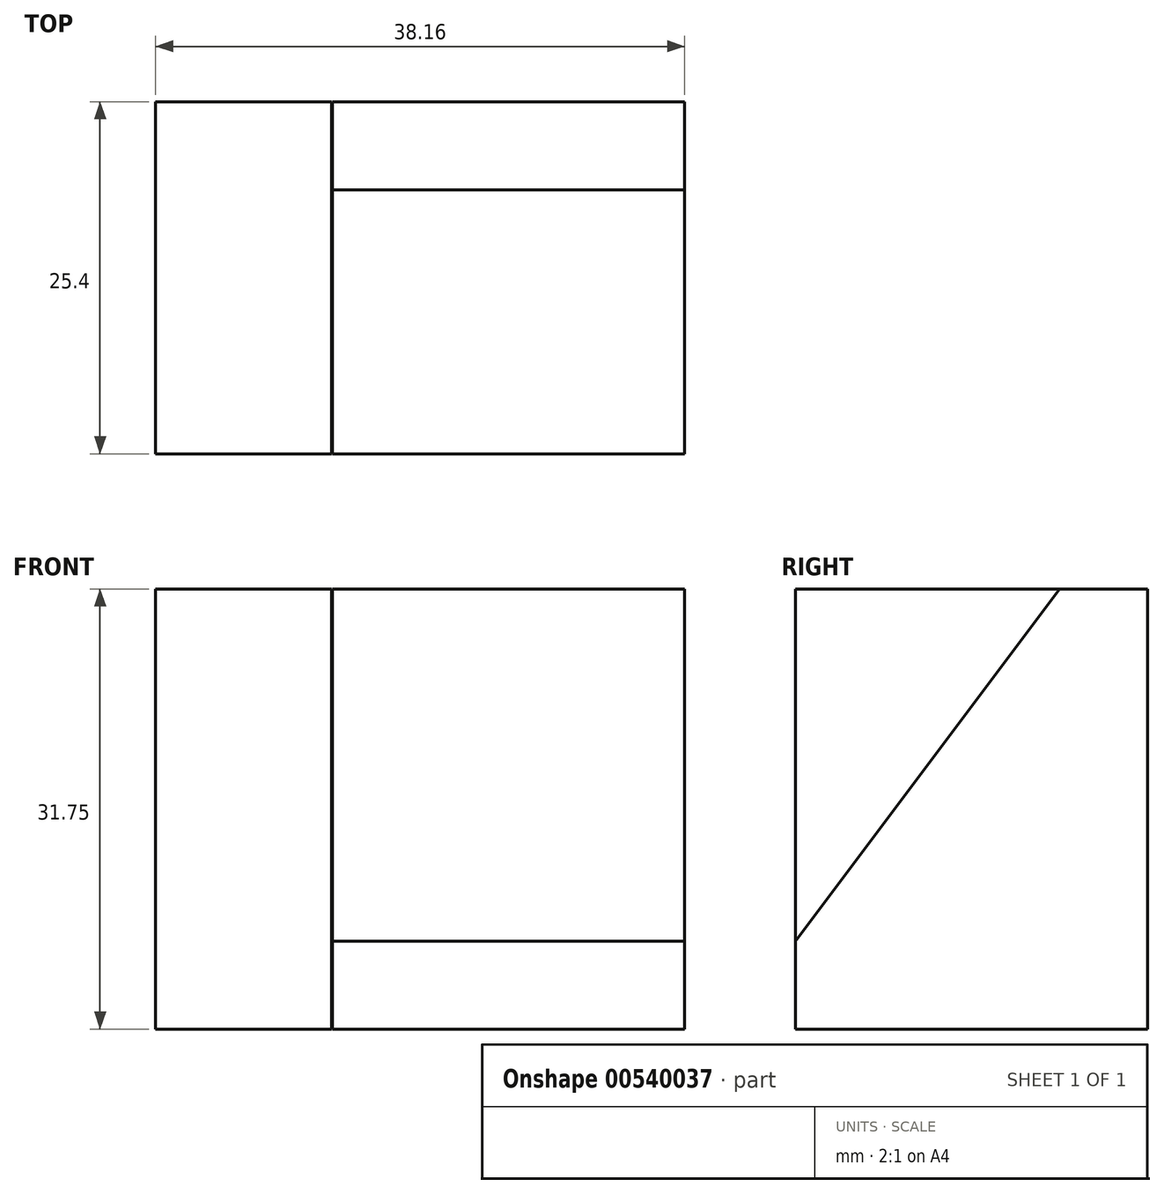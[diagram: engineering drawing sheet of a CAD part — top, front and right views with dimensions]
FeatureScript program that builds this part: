
annotation { "Feature Type Name" : "Feature", "Feature Type Description" : "" }
export const myFeature = defineFeature(function(context is Context, id is Id, definition is map)
    precondition{}
    {
        {
            var Q0;
            Q0=qCreatedBy(makeId("Right.planeOp"),FACE);
            var sketch = newSketch(context, id + "F0", { "sketchPlane" : qUnion([Q0])});
            skLineSegment(sketch, "E0", {"start": v(0, 0) * mm, "end": v(25.4, 0) * mm});
            skLineSegment(sketch, "E1", {"start": v(25.4, 0) * mm, "end": v(25.4, 31.75) * mm});
            skLineSegment(sketch, "E2", {"start": v(25.4, 31.75) * mm, "end": v(19.05, 31.75) * mm});
            skLineSegment(sketch, "E3", {"start": v(0, 0) * mm, "end": v(0, 6.35) * mm});
            skLineSegment(sketch, "E4", {"start": v(0, 6.35) * mm, "end": v(19.05, 31.75) * mm});
            skSolve(sketch);
        }
        {
            var Q0;
            Q0 = qSketchRegion(id + "F0", true);
            extrude(context, id + "F1", {"entities" : qUnion([Q0]), "oppositeDirection" : true, "depth" : 25.4 * mm, "offsetDistance" : 25.4 * mm});
        }
        {
            var Q0;
            Q0=qCreatedBy(makeId("Front.planeOp"),FACE);
            var sketch = newSketch(context, id + "F2", { "sketchPlane" : qUnion([Q0])});
            skLineSegment(sketch, "E5", {"start": v(-25.46, 0) * mm, "end": v(-25.46, 31.75) * mm});
            skLineSegment(sketch, "E6", {"start": v(-25.46, 31.75) * mm, "end": v(-38.16, 31.75) * mm});
            skLineSegment(sketch, "E7", {"start": v(-38.16, 31.75) * mm, "end": v(-38.16, 0) * mm});
            skLineSegment(sketch, "E8", {"start": v(-38.16, 0) * mm, "end": v(-25.46, 0) * mm});
            skSolve(sketch);
        }
        {
            var Q0;
            Q0 = qSketchRegion(id + "F2", true);
            extrude(context, id + "F3", {"entities" : qUnion([Q0]), "oppositeDirection" : true, "depth" : 25.4 * mm, "offsetDistance" : 25.4 * mm});
        }
    });
